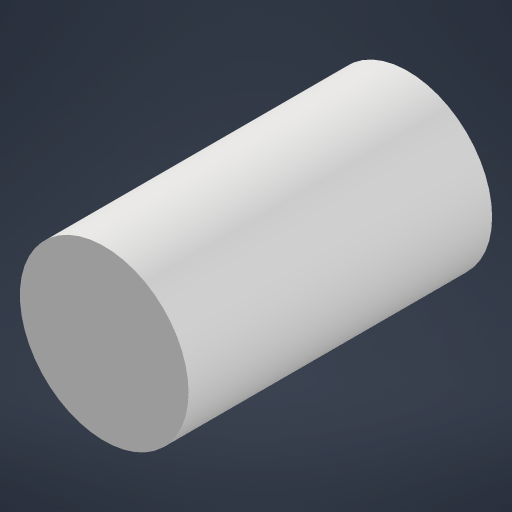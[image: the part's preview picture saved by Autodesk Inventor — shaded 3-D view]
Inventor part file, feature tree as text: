
AUTODESK INVENTOR PART (.ipt)
format: ipt  version: 2024 (Build 280153000, 153)  size: 164,864 bytes
history: native  units: mm
features: other x1, extrude x1, sketch x1
ambient origin geometry x8: Origin, YZ Plane, XZ Plane, XY Plane, X Axis, Y Axis, Z Axis, Center Point
bodies: Body1 (feature_tree)
feature tree (3):
  other  "Sólido1"
  extrude  "Extrusión1"  Depth=18.0mm TaperAngle=0.0deg
  sketch  "Boceto1"  dims[d0=10.0mm d1=18.0mm d2=0.0mm]
